# Revit family: VL2S-GFS100xSWxBQPx
name_source: partatom
category: Leuchten
units: mm (PartAtom-declared; Revit-internal decimal feet)

## family parameters
Basisbauteil = Fläche
Beim Laden mit Abzugskörper schneiden = Nein
Bemaßung runder Anschluss = Durchmesser verwenden
Gemeinsam genutzt = Nein
Lichtquelle = Ja
OmniClass-Nummer = 23.80.70.11
OmniClass-Titel = Luminaries for Internal Lighting
Raumberechnungspunkt = Nein
Teiletyp = Normal

## types (8) — shared parameters
Baugruppenkennzeichen = D5020200
Datei für fotometrisches Netz = VL2S-GFS_BQP.IES
Emissionsform beim Rendern sichtbar = Nein
Farbfilter = 16777215
Farbtemperaturverschiebung bei Dämpfen der Lampe = <Keine Auswahl>
Hersteller = RIDI Leuchten GmbH
Lampe = LED
Neigungswinkel = 90.00°
URL = www.ridi.de
Von Breite des Rechtecks ausssenden = 976 mm  [stored 3.2021 ft]
Von Länge des Rechtecks aussenden = 85 mm  [stored 0.278871 ft]
brand = RIDI
conformity mark = CE
electrical safety class = 1
height = 77 mm  [stored 0.252625 ft]
ingress protection (IP) code = IP54
length = 1000 mm  [stored 3.28084 ft]
nominal frequency = 50-60Hz
nominal voltage = 230
voltage type (AC, DC, UC) = AC
weight = 2,1 kg
width = 97 mm  [stored 0.318241 ft]
zero-valued in all types: Vorgabe-Ansicht

## per-type parameters (varying)
| type | Modell | Scheinlast | rated input power |
| VL2S-GFS100-5FLSW840BQP0500 | 2550146SW | 35 VA | 35 |
| VL2S-GFS100-5FLSW830BQP0500 | 2550167SW | 35 VA | 35 |
| VL2S-GFS100-5FLSW850BQP0500 | 2550170SW | 35 VA | 35 |
| VL2S-GFS100-5FLSW865BQP0500 | 2550173SW | 35 VA | 35 |
| VL2S-GFS100-7DASW840BQP0500 | 2560146SW | 36 VA | 36 |
| VL2S-GFS100-7DASW830BQP0500 | 2560167SW | 36 VA | 36 |
| VL2S-GFS100-7DASW850BQP0500 | 2560170SW | 36 VA | 36 |
| VL2S-GFS100-7DASW865BQP0500 | 2560173SW | 36 VA | 36 |

note: column(s) folded — value = type name in every type: product name

note: [stored X ft] marks values corroborated as IEEE doubles in the binary element streams (Revit-internal decimal feet)
